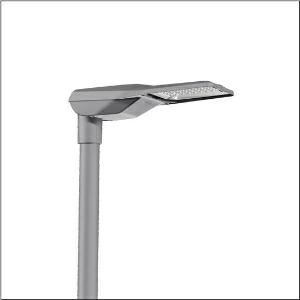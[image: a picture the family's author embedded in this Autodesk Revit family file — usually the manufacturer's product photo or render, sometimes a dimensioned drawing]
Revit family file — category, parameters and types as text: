
# Revit family: streetlight_sl_21_iq_mini___st0_5a_5xe2b41d08gb_120c
name_source: partatom
category: Lighting Fixtures
units: mm (PartAtom-declared; Revit-internal decimal feet)

## family parameters
Cut with Voids When Loaded = No
Host = Face
Light Source = No
Part Type = Normal
Room Calculation Point = No
Round Connector Dimension = Use Diameter
Shared = No

## types (1)
- --- (1 x LED, 5920 lm, 37.1 W, 4000K)
    Apparent Load = 37 VA
    CIE Flux Codes = 41 75 97 100 100
    Color Rendering = 70
    Color Temperature = 4000K
    Default Elevation = 1800 mm
    Description = Streetlight SL 21 iQ mini, mast luminaire, primary light control with lens, of PMMA, primary optical cover: cover, of toughened safety glass, transparent, light distribution: ST0.5a, light emission: direct distribution, primary light characteristic: asymmetric, installation type: post-top, side-entry, LED, High Power LED, rated luminous flux: 5.920lm, luminous efficacy: 160lm/W, light colour: 740, colour temperature: 4000K, control: Auto-Match, Temp-Guard, Lumen-Switch, Night-Set, Smart-Wire, Light-Fading, Desk-Remote (wireless, voltage-free reading and setting of iQ features in the workshop via application-optimized NFC function/RFID function), optimised constant luminous flux control (CLO 2.0), presetting dimming linear, mains connection: 220..240V, AC, 50/60Hz, start of lifetime: 37W, end of service life: 39W, reduction: 18W, luminaire housing, of diecast aluminium, powder-coated, Siteco® metallic grey (DB 702S), corrosivity category C5 mid according to DIN EN ISO 12944, please order mast flange separately, inclination adjustable: 0°, 5°, 10°, 15°, sealing non-destructively replaceable, multi-level sealing system, length: 628mm, width: 235mm, height: 110mm, mast flange for spigot size: 42mm (side-entry): 5XC10008XM4, 60/48mm (side-entry/post-top): 5XC10108XM2, 76/60mm (side-entry/post-top): 5XC10108XM1, protection rating (complete): IP66, insulation class (complete): insulation class II (safety insulation), certification: CE, ENEC, ENEC+, VDE, impact resistance: IK09, permissible operating ambient temperature for outdoor applications: -40..+50°C, standard-compliant lighting for roads and squares, packaging unit: 1 piece

Light Distribution: ST0.5a
    Height = 110 mm
    Lamp = 1 x LED
    Lamp Light Flux = 5920 lm
    Lamp Power = 37.1 W
    Lamp count = 1
    Length = 625 mm
    Luminous efficacy = 160 lm/W
    Manufacturer = Siteco
    ModVariant = No
    Model = 5XE2B41D08GB
    Number of Poles = 1
    OnlyDefault = Yes
    Power Factor = 1
    Product Name = Streetlight SL 21 iQ mini | ST0.5a
    Product group = mast luminaire | pylon top
    ProductGroupID = 6100
    Protection Class = Protection class II
    Protection Degree = IP 66
    RLX_Detail_Level = 1
    RLX_Emergency_Light_Flux = 0 lm
    RLX_Emergency_Type = 0
    RLX_Emergency_Type_DB = No
    RlxData = <blob elided: 103245 chars, md5=a7dec872>
    Socket = socket
    Standby Power = 0 W
    System Light Flux = 5920 lm
    System Power = 37 W
    Type Comments = factory setting: luminous flux: 100 % | dim-lin: 254 | 385 mA
    Type Image = l_1003519.jpg
    URL = http://relux.com
    VarID = @adj_125481
    Voltage = 0 V
    Weight = 0.00 kg
    Width = 234 mm

## geometry (parser evidence)
native form markers: Blend x4, Sweep x11
no freeform markers — native parametric forms only
